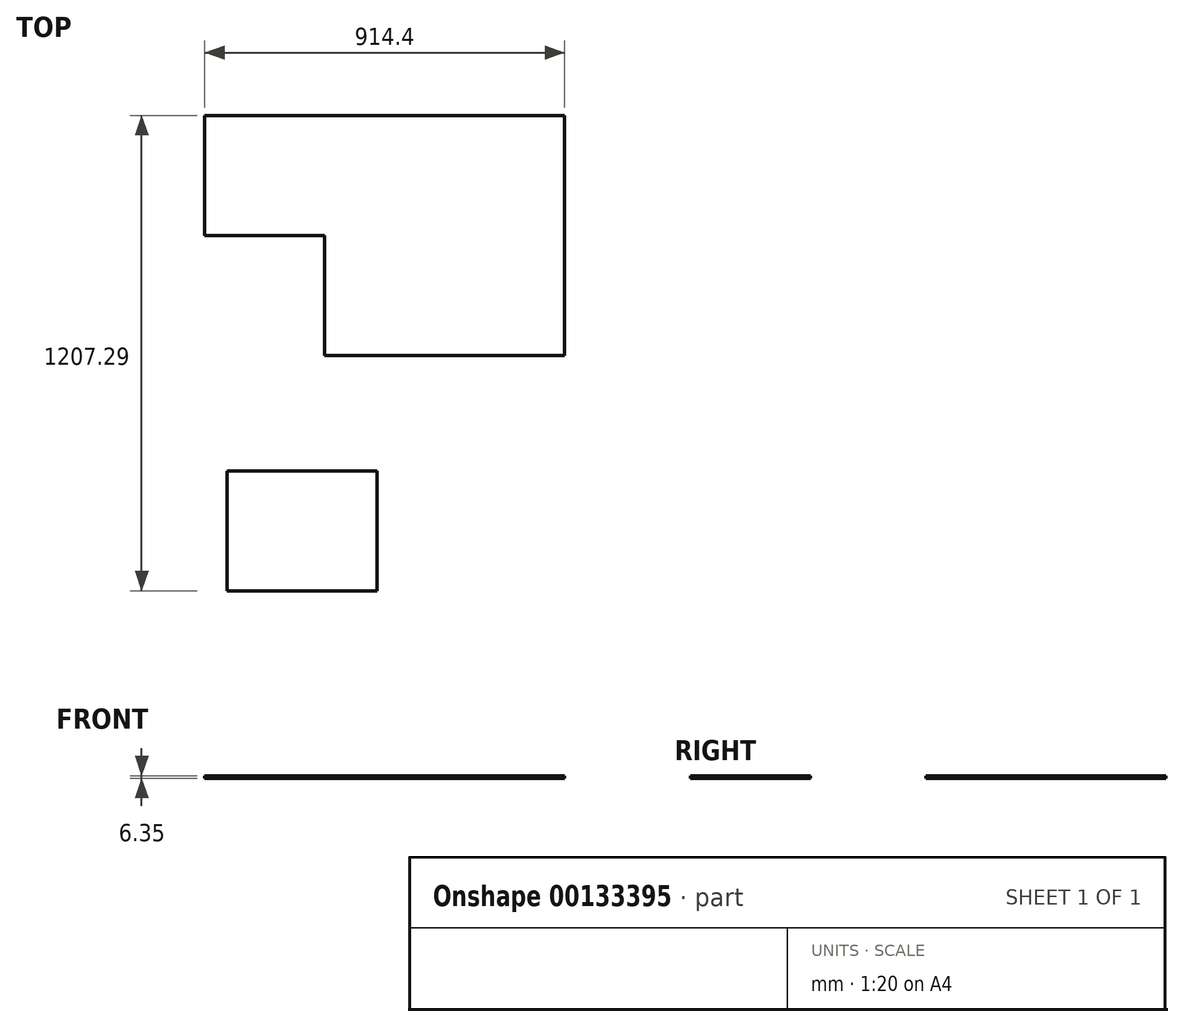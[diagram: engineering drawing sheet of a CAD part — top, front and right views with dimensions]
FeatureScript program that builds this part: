
annotation { "Feature Type Name" : "Feature", "Feature Type Description" : "" }
export const myFeature = defineFeature(function(context is Context, id is Id, definition is map)
    precondition{}
    {
        {
            var Q0;
            Q0=qCreatedBy(makeId("Top.planeOp"),FACE);
            var sketch = newSketch(context, id + "F0", { "sketchPlane" : qUnion([Q0])});
            skLineSegment(sketch, "E0.bottom", {"start": v(304.8, -304.8) * mm, "end": v(-304.8, -304.8) * mm});
            skLineSegment(sketch, "E0.top", {"start": v(304.8, 304.8) * mm, "end": v(-304.8, 304.8) * mm});
            skLineSegment(sketch, "E0.left", {"start": v(304.8, -304.8) * mm, "end": v(304.8, 304.8) * mm});
            skLineSegment(sketch, "E0.right", {"start": v(-304.8, -304.8) * mm, "end": v(-304.8, 304.8) * mm});
            skPoint(sketch, "E0.middle", {"position": v(0, 0) * mm});
            skSolve(sketch);
        }
        {
            var Q0;
            Q0=makeQuery(id+"F0.imprint","IMPRINT",FACE,{"disambiguationData":[TD([[makeQuery(id+"F0.imprint","IMPRINT",EDGE,{"derivedFrom":sQuery(id+"F0.wireOp",EDGE,"E0.bottom")}),-1.0]])]});
            extrude(context, id + "F1", {"entities" : qUnion([Q0]), "depth" : 6.35 * mm});
        }
        {
            var Q0;
            Q0=makeQuery(id+"F1.opExtrude","SWEPT_FACE",FACE,{"disambiguationData":[OSD([sQuery(id+"F0.wireOp",EDGE,"E0.right")])]});
            var sketch = newSketch(context, id + "F2", { "sketchPlane" : qUnion([Q0])});
            skLineSegment(sketch, "E1.bottom", {"start": v(-304.8, 0) * mm, "end": v(0, 0) * mm});
            skLineSegment(sketch, "E1.top", {"start": v(-304.8, 6.35) * mm, "end": v(0, 6.35) * mm});
            skLineSegment(sketch, "E1.left", {"start": v(-304.8, 0) * mm, "end": v(-304.8, 6.35) * mm});
            skLineSegment(sketch, "E1.right", {"start": v(0, 0) * mm, "end": v(0, 6.35) * mm});
            skSolve(sketch);
        }
        {
            var Q0;
            Q0 = qSketchRegion(id + "F2", true);
            extrude(context, id + "F3", {"entities" : qUnion([Q0]), "operationType" : NewBodyOperationType.ADD, "depth" : 304.8 * mm});
        }
        {
            var Q0;
            Q0=qCreatedBy(makeId("Top.planeOp"),FACE);
            var sketch = newSketch(context, id + "F4", { "sketchPlane" : qUnion([Q0])});
            skLineSegment(sketch, "E2.bottom", {"start": v(-553.02, -597.7) * mm, "end": v(-172.02, -597.7) * mm});
            skLineSegment(sketch, "E2.top", {"start": v(-553.02, -902.5) * mm, "end": v(-172.02, -902.5) * mm});
            skLineSegment(sketch, "E2.left", {"start": v(-553.02, -597.7) * mm, "end": v(-553.02, -902.5) * mm});
            skLineSegment(sketch, "E2.right", {"start": v(-172.02, -597.7) * mm, "end": v(-172.02, -902.5) * mm});
            skSolve(sketch);
        }
        {
            var Q0;
            Q0 = qSketchRegion(id + "F4", true);
            extrude(context, id + "F5", {"entities" : qUnion([Q0]), "depth" : 6.35 * mm});
        }
    });
